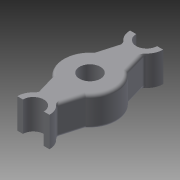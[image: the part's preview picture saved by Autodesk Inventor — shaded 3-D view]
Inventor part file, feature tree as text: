
AUTODESK INVENTOR PART (.ipt)
format: ipt  version: 2015 (Build 190159000, 159)  size: 285,696 bytes
history: native  units: in
note: dims shown in document units (in); Inventor stores cm internally (conversion verified against a paired STEP export)
features: extrude x3, sketch x3, fillet x2
ambient origin geometry x8: Origin, YZ Plane, XZ Plane, XY Plane, X Axis, Y Axis, Z Axis, Center Point
bodies: Solid1 (feature_tree)
feature tree (8):
  extrude  "Extrusion1"  Depth=14.9606in
  extrude  "Extrusion2"  Depth=2.7559in
  fillet  "Fillet1"  Radius=7.0866in
  fillet  "Fillet2"  Radius=0.7548in
  extrude  "Extrusion3"  Depth=0.3937in
  sketch  "Sketch1"  dims[d0=7.4803in d1=14.9606in]
  sketch  "Sketch2"  dims[d2=2.7559in d3=2.7559in d4=7.0866in d11=0.7548in d12=0.81in]
  sketch  "Sketch3"  dims[d14=3.937in d15=0.0in d16=2.7559in d17=1.9685in d18=0.0in d19=0.3937in d20=0.3937in d21=5.1181in d22=0.3937in d23=0.0in]
